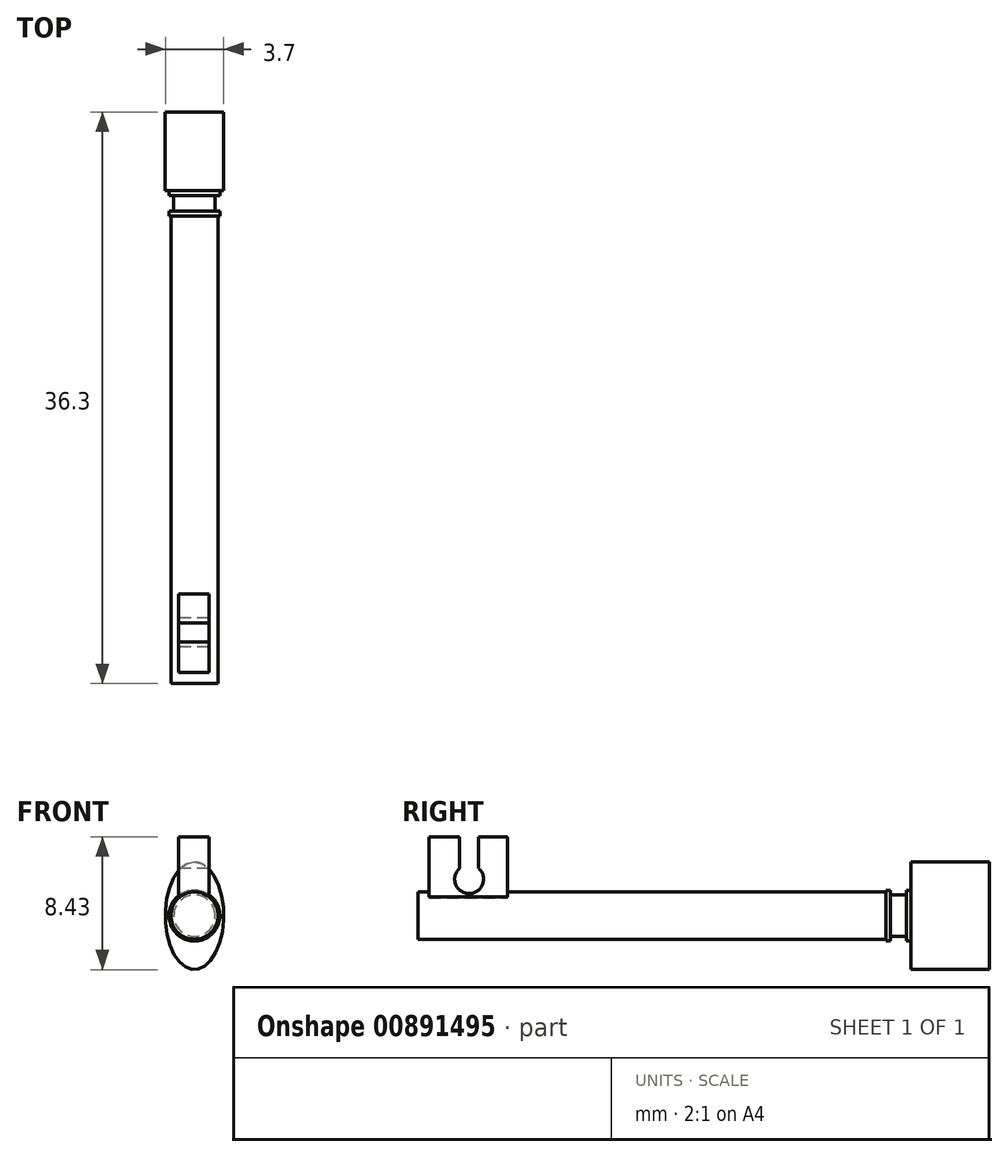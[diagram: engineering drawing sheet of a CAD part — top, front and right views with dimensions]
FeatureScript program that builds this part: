
annotation { "Feature Type Name" : "Feature", "Feature Type Description" : "" }
export const myFeature = defineFeature(function(context is Context, id is Id, definition is map)
    precondition{}
    {
        {
            var Q0;
            Q0=qCreatedBy(makeId("Front.planeOp"),FACE);
            var sketch = newSketch(context, id + "F0", { "sketchPlane" : qUnion([Q0])});
            skCircle(sketch, "E0", {"center": v(0, 0) * mm, "radius": 1.5 * mm});
            skSolve(sketch);
        }
        {
            var Q0;
            Q0 = qSketchRegion(id + "F0", true);
            extrude(context, id + "F1", {"entities" : qUnion([Q0]), "depth" : 30 * mm, "offsetDistance" : 25 * mm});
        }
        {
            var Q0;
            Q0=qCreatedBy(makeId("Front.planeOp"),FACE);
            var sketch = newSketch(context, id + "F2", { "sketchPlane" : qUnion([Q0])});
            skCircle(sketch, "E1", {"center": v(0, 0) * mm, "radius": 1.61 * mm});
            skSolve(sketch);
        }
        {
            var Q0;
            Q0 = qSketchRegion(id + "F2", true);
            extrude(context, id + "F3", {"entities" : qUnion([Q0]), "operationType" : NewBodyOperationType.ADD, "depth" : 0.3 * mm, "offsetDistance" : 25 * mm});
        }
        {
            var Q0;
            Q0=makeQuery(id+"F3.boolean.opBoolean","MERGE",FACE,{"derivedFrom":[makeQuery(id+"F1.opExtrude","CAP_FACE",FACE,{"disambiguationData":[OSD([sQuery(id+"F0.wireOp",EDGE,"E0")])],"isStart":true}),makeQuery(id+"F3.opExtrude","CAP_FACE",FACE,{"disambiguationData":[OSD([sQuery(id+"F2.wireOp",EDGE,"E1")])],"isStart":true})]});
            var sketch = newSketch(context, id + "F4", { "sketchPlane" : qUnion([Q0])});
            skCircle(sketch, "E2", {"center": v(0, 0) * mm, "radius": 1.31 * mm});
            skSolve(sketch);
        }
        {
            var Q0;
            Q0 = qSketchRegion(id + "F4", true);
            extrude(context, id + "F5", {"entities" : qUnion([Q0]), "operationType" : NewBodyOperationType.ADD, "depth" : 1 * mm, "offsetDistance" : 25 * mm});
        }
        {
            var Q0;
            Q0=makeQuery(id+"F5.opExtrude","CAP_FACE",FACE,{"disambiguationData":[OSD([sQuery(id+"F4.wireOp",EDGE,"E2")])],"isStart":false});
            var sketch = newSketch(context, id + "F6", { "sketchPlane" : qUnion([Q0])});
            skCircle(sketch, "E3", {"center": v(0, 0) * mm, "radius": 1.61 * mm});
            skSolve(sketch);
        }
        {
            var Q0;
            Q0 = qSketchRegion(id + "F6", true);
            extrude(context, id + "F7", {"entities" : qUnion([Q0]), "operationType" : NewBodyOperationType.ADD, "depth" : 0.3 * mm, "offsetDistance" : 25 * mm});
        }
        {
            var Q0;
            Q0=qCreatedBy(makeId("Top.planeOp"),FACE);
            var sketch = newSketch(context, id + "F8", { "sketchPlane" : qUnion([Q0])});
            skLineSegment(sketch, "E4.bottom", {"start": v(-1, -24.32) * mm, "end": v(0.92, -24.32) * mm});
            skLineSegment(sketch, "E4.top", {"start": v(-1, -29.32) * mm, "end": v(0.92, -29.32) * mm});
            skLineSegment(sketch, "E4.left", {"start": v(-1, -24.32) * mm, "end": v(-1, -29.32) * mm});
            skLineSegment(sketch, "E4.right", {"start": v(0.92, -24.32) * mm, "end": v(0.92, -29.32) * mm});
            skSolve(sketch);
        }
        {
            var Q0;
            Q0 = qSketchRegion(id + "F8", true);
            extrude(context, id + "F9", {"entities" : qUnion([Q0]), "operationType" : NewBodyOperationType.ADD, "depth" : 5 * mm, "offsetDistance" : 25 * mm});
        }
        {
            var Q0;
            Q0=makeQuery(id+"F9.opExtrude","SWEPT_FACE",FACE,{"disambiguationData":[OSD([sQuery(id+"F8.wireOp",EDGE,"E4.left")])]});
            var sketch = newSketch(context, id + "F10", { "sketchPlane" : qUnion([Q0])});
            skLineSegment(sketch, "E5.bottom", {"start": v(26.16, 5) * mm, "end": v(27.36, 5) * mm});
            skLineSegment(sketch, "E5.top", {"start": v(26.16, 2.42) * mm, "end": v(27.36, 2.42) * mm});
            skLineSegment(sketch, "E5.left", {"start": v(26.16, 5) * mm, "end": v(26.16, 2.42) * mm});
            skLineSegment(sketch, "E5.right", {"start": v(27.36, 5) * mm, "end": v(27.36, 2.42) * mm});
            skCircle(sketch, "E6", {"center": v(26.76, 2.32) * mm, "radius": 0.92 * mm});
            skPoint(sketch, "E6.centerSnap0", {"position": v(26.76, 2.42) * mm});
            skSolve(sketch);
        }
        {
            var Q0;
            Q0 = qSketchRegion(id + "F10", true);
            extrude(context, id + "F11", {"entities" : qUnion([Q0]), "operationType" : NewBodyOperationType.REMOVE, "oppositeDirection" : true, "depth" : 25 * mm, "offsetDistance" : 25 * mm});
        }
        {
            var Q0;
            Q0=makeQuery(id+"F7.opExtrude","CAP_FACE",FACE,{"disambiguationData":[OSD([sQuery(id+"F6.wireOp",EDGE,"E3")])],"isStart":false});
            var sketch = newSketch(context, id + "F12", { "sketchPlane" : qUnion([Q0])});
            skEllipse(sketch, "E7", {"center": v(0, 0) * mm, "majorRadius": 3.43 * mm, "minorRadius": 1.85 * mm, "majorAxis": v(0, 1)});
            skSolve(sketch);
        }
        {
            var Q0;
            Q0 = qSketchRegion(id + "F12", true);
            extrude(context, id + "F13", {"entities" : qUnion([Q0]), "operationType" : NewBodyOperationType.ADD, "depth" : 5 * mm, "offsetDistance" : 25 * mm});
        }
    });
